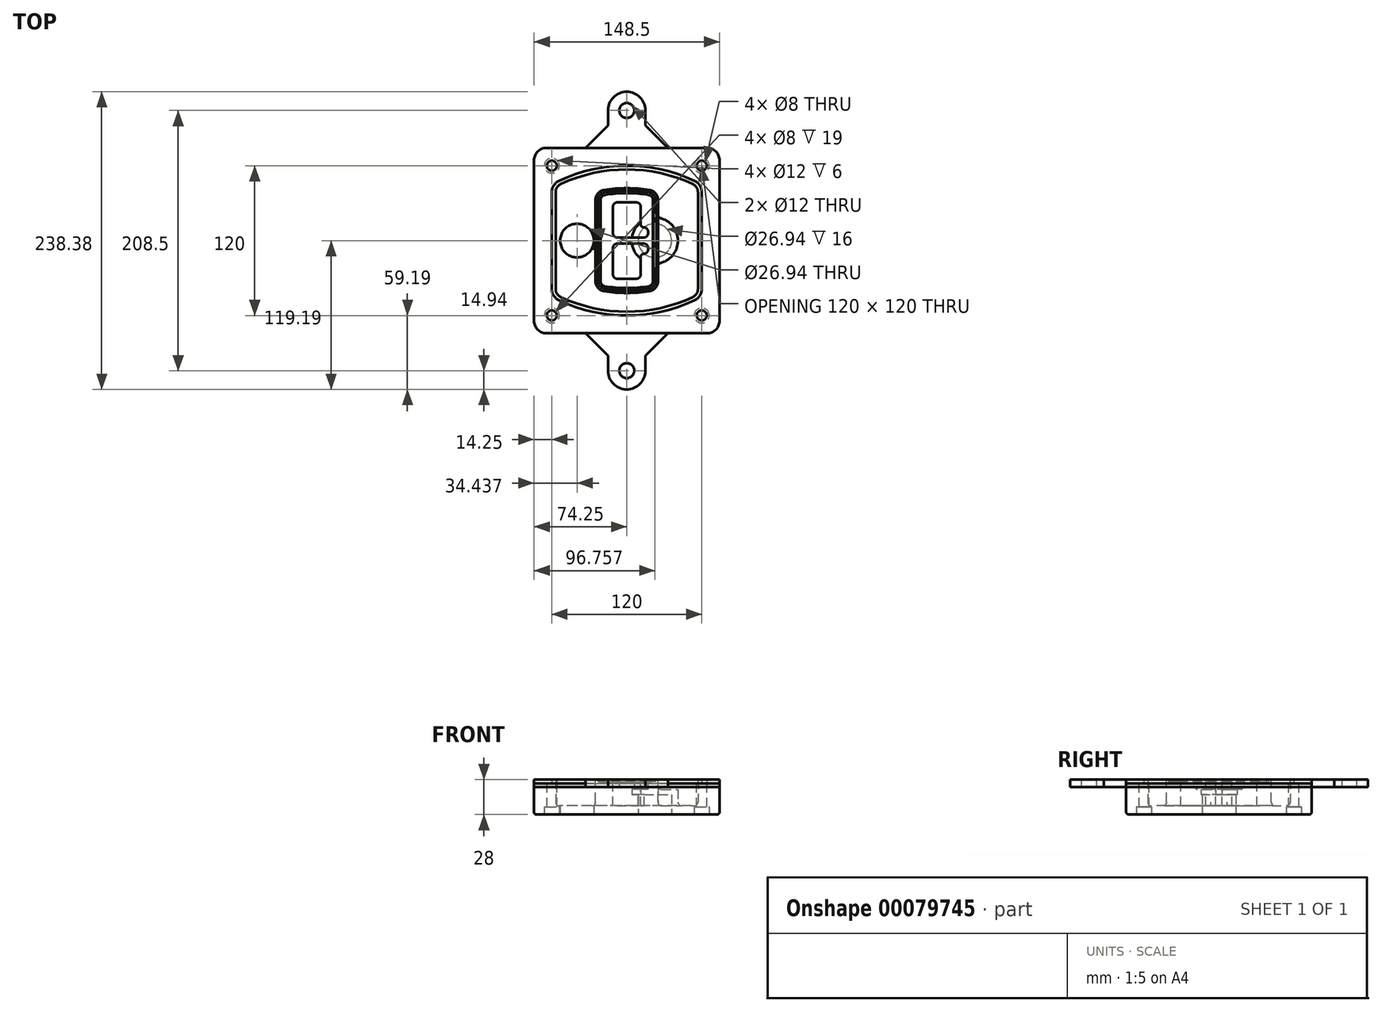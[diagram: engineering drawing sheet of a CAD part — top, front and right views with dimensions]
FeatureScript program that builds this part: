
annotation { "Feature Type Name" : "Feature", "Feature Type Description" : "" }
export const myFeature = defineFeature(function(context is Context, id is Id, definition is map)
    precondition{}
    {
        {
            var Q0;
            Q0=qCreatedBy(makeId("Top.planeOp"),FACE);
            var sketch = newSketch(context, id + "F0", { "sketchPlane" : qUnion([Q0])});
            skPoint(sketch, "E0.rect.middle", {"position": v(0, 0) * mm});
            skLineSegment(sketch, "E1.bottom", {"start": v(-64.25, -74.25) * mm, "end": v(64.25, -74.25) * mm});
            skLineSegment(sketch, "E1.top", {"start": v(-64.25, 74.25) * mm, "end": v(64.25, 74.25) * mm});
            skLineSegment(sketch, "E1.left", {"start": v(-74.25, -64.25) * mm, "end": v(-74.25, 64.25) * mm});
            skLineSegment(sketch, "E1.right", {"start": v(74.25, -64.25) * mm, "end": v(74.25, 64.25) * mm});
            skLineSegment(sketch, "E2", {"start": v(-74.25, 74.25) * mm, "end": v(74.25, -74.25) * mm, "construction": true});
            skLineSegment(sketch, "E3", {"start": v(74.25, 74.25) * mm, "end": v(-74.25, -74.25) * mm, "construction": true});
            skCircle(sketch, "E4", {"center": v(-60, 60) * mm, "radius": 4 * mm});
            skCircle(sketch, "E5", {"center": v(60, 60) * mm, "radius": 4 * mm});
            skCircle(sketch, "E6", {"center": v(60, -60) * mm, "radius": 4 * mm});
            skCircle(sketch, "E7", {"center": v(-60, -60) * mm, "radius": 4 * mm});
            skLineSegment(sketch, "E8", {"start": v(-60, 60) * mm, "end": v(60, 60) * mm, "construction": true});
            skLineSegment(sketch, "E9", {"start": v(60, 60) * mm, "end": v(60, -60) * mm, "construction": true});
            skLineSegment(sketch, "E10", {"start": v(60, -60) * mm, "end": v(-60, -60) * mm, "construction": true});
            skLineSegment(sketch, "E11", {"start": v(-60, -60) * mm, "end": v(-60, 60) * mm, "construction": true});
            skLineSegment(sketch, "E12", {"start": v(-60, 38.83) * mm, "end": v(-60, -38.83) * mm});
            skLineSegment(sketch, "E13", {"start": v(60, 38.83) * mm, "end": v(60, -38.83) * mm});
            skArc(sketch, "E14", {"start": v(54.26, 47.88) * mm, "mid": v(0, 60) * mm, "end": v(-54.26, 47.88) * mm});
            skArc(sketch, "E15", {"start": v(-54.26, -47.88) * mm, "mid": v(0, -60) * mm, "end": v(54.26, -47.88) * mm});
            skLineSegment(sketch, "E16", {"start": v(-60, 0) * mm, "end": v(60, 0) * mm, "construction": true});
            skPoint(sketch, "E17.visualSharp", {"position": v(-60, -45) * mm});
            skArc(sketch, "E17.filletArc", {"start": v(-60, -38.83) * mm, "mid": v(-58.44, -44.2) * mm, "end": v(-54.26, -47.88) * mm});
            skPoint(sketch, "E18.visualSharp", {"position": v(-60, 45) * mm});
            skArc(sketch, "E18.filletArc", {"start": v(-54.26, 47.88) * mm, "mid": v(-58.44, 44.2) * mm, "end": v(-60, 38.83) * mm});
            skPoint(sketch, "E19.visualSharp", {"position": v(60, 45) * mm});
            skArc(sketch, "E19.filletArc", {"start": v(60, 38.83) * mm, "mid": v(58.44, 44.2) * mm, "end": v(54.26, 47.88) * mm});
            skPoint(sketch, "E20.visualSharp", {"position": v(60, -45) * mm});
            skArc(sketch, "E20.filletArc", {"start": v(54.26, -47.88) * mm, "mid": v(58.44, -44.2) * mm, "end": v(60, -38.83) * mm});
            skPoint(sketch, "E21.visualSharp", {"position": v(-74.25, 74.25) * mm});
            skArc(sketch, "E21.filletArc", {"start": v(-64.25, 74.25) * mm, "mid": v(-71.32, 71.32) * mm, "end": v(-74.25, 64.25) * mm});
            skPoint(sketch, "E22.visualSharp", {"position": v(74.25, 74.25) * mm});
            skArc(sketch, "E22.filletArc", {"start": v(74.25, 64.25) * mm, "mid": v(71.32, 71.32) * mm, "end": v(64.25, 74.25) * mm});
            skPoint(sketch, "E23.visualSharp", {"position": v(74.25, -74.25) * mm});
            skArc(sketch, "E23.filletArc", {"start": v(64.25, -74.25) * mm, "mid": v(71.32, -71.32) * mm, "end": v(74.25, -64.25) * mm});
            skPoint(sketch, "E24.visualSharp", {"position": v(-74.25, -74.25) * mm});
            skArc(sketch, "E24.filletArc", {"start": v(-74.25, -64.25) * mm, "mid": v(-71.32, -71.32) * mm, "end": v(-64.25, -74.25) * mm});
            skArc(sketch, "E25.0", {"start": v(57, 38.83) * mm, "mid": v(55.9, 42.58) * mm, "end": v(52.98, 45.17) * mm});
            skLineSegment(sketch, "E25.1", {"start": v(57, 38.83) * mm, "end": v(57, -38.83) * mm});
            skArc(sketch, "E25.2", {"start": v(52.98, -45.17) * mm, "mid": v(55.9, -42.58) * mm, "end": v(57, -38.83) * mm});
            skArc(sketch, "E25.3", {"start": v(-52.98, -45.17) * mm, "mid": v(0, -57) * mm, "end": v(52.98, -45.17) * mm});
            skArc(sketch, "E25.4", {"start": v(-57, -38.83) * mm, "mid": v(-55.9, -42.58) * mm, "end": v(-52.98, -45.17) * mm});
            skArc(sketch, "E25.5", {"start": v(52.98, 45.17) * mm, "mid": v(0, 57) * mm, "end": v(-52.98, 45.17) * mm});
            skLineSegment(sketch, "E25.6", {"start": v(-57, 38.83) * mm, "end": v(-57, -38.83) * mm});
            skArc(sketch, "E25.7", {"start": v(-52.98, 45.17) * mm, "mid": v(-55.9, 42.58) * mm, "end": v(-57, 38.83) * mm});
            skArc(sketch, "E26.0", {"start": v(-55.96, 51.5) * mm, "mid": v(-61.82, 46.33) * mm, "end": v(-64, 38.83) * mm});
            skArc(sketch, "E26.1", {"start": v(55.96, 51.5) * mm, "mid": v(0, 64) * mm, "end": v(-55.96, 51.5) * mm});
            skArc(sketch, "E26.2", {"start": v(64, 38.83) * mm, "mid": v(61.82, 46.33) * mm, "end": v(55.96, 51.5) * mm});
            skLineSegment(sketch, "E26.3", {"start": v(64, 38.83) * mm, "end": v(64, -38.83) * mm});
            skArc(sketch, "E26.4", {"start": v(55.96, -51.5) * mm, "mid": v(61.82, -46.33) * mm, "end": v(64, -38.83) * mm});
            skLineSegment(sketch, "E26.5", {"start": v(-64, 38.83) * mm, "end": v(-64, -38.83) * mm});
            skArc(sketch, "E26.6", {"start": v(-55.96, -51.5) * mm, "mid": v(0, -64) * mm, "end": v(55.96, -51.5) * mm});
            skArc(sketch, "E26.7", {"start": v(-64, -38.83) * mm, "mid": v(-61.82, -46.33) * mm, "end": v(-55.96, -51.5) * mm});
            skSolve(sketch);
        }
        {
            var Q0;
            Q0=makeQuery(id+"F0.imprint","IMPRINT",FACE,{"disambiguationData":[TD([[makeQuery(id+"F0.imprint","IMPRINT",EDGE,{"derivedFrom":sQuery(id+"F0.wireOp",EDGE,"E1.bottom")}),1.0]])]});
            var Q1;
            Q1=makeQuery(id+"F0.imprint","IMPRINT",FACE,{"disambiguationData":[TD([[makeQuery(id+"F0.imprint","IMPRINT",EDGE,{"derivedFrom":sQuery(id+"F0.wireOp",EDGE,"E12")}),1.0]])]});
            var Q2;
            Q2=makeQuery(id+"F0.imprint","IMPRINT",FACE,{"disambiguationData":[TD([[makeQuery(id+"F0.imprint","IMPRINT",EDGE,{"derivedFrom":sQuery(id+"F0.wireOp",EDGE,"E25.0")}),1.0]])]});
            var Q3;
            Q3=makeQuery(id+"F0.imprint","IMPRINT",FACE,{"disambiguationData":[TD([[makeQuery(id+"F0.imprint","IMPRINT",EDGE,{"derivedFrom":sQuery(id+"F0.wireOp",EDGE,"E12")}),-1.0]])]});
            extrude(context, id + "F1", {"entities" : qUnion([Q0, Q1, Q2, Q3]), "oppositeDirection" : true, "depth" : 25 * mm});
        }
        {
            var Q0;
            Q0=makeQuery(id+"F0.imprint","IMPRINT",FACE,{"disambiguationData":[TD([[makeQuery(id+"F0.imprint","IMPRINT",EDGE,{"derivedFrom":sQuery(id+"F0.wireOp",EDGE,"E12")}),1.0]])]});
            extrude(context, id + "F2", {"entities" : qUnion([Q0]), "operationType" : NewBodyOperationType.ADD, "depth" : 3 * mm});
        }
        {
            var Q0;
            Q0=makeQuery(id+"F0.imprint","IMPRINT",FACE,{"disambiguationData":[TD([[makeQuery(id+"F0.imprint","IMPRINT",EDGE,{"derivedFrom":sQuery(id+"F0.wireOp",EDGE,"E25.0")}),1.0]])]});
            extrude(context, id + "F3", {"entities" : qUnion([Q0]), "operationType" : NewBodyOperationType.REMOVE, "oppositeDirection" : true, "depth" : 18 * mm});
        }
        {
            var Q0;
            Q0=makeQuery(id+"F2.opExtrude","CAP_FACE",FACE,{"disambiguationData":[OSD([sQuery(id+"F0.wireOp",EDGE,"E12"),sQuery(id+"F0.wireOp",EDGE,"E13"),sQuery(id+"F0.wireOp",EDGE,"E14"),sQuery(id+"F0.wireOp",EDGE,"E15"),sQuery(id+"F0.wireOp",EDGE,"E17.filletArc"),sQuery(id+"F0.wireOp",EDGE,"E18.filletArc"),sQuery(id+"F0.wireOp",EDGE,"E19.filletArc"),sQuery(id+"F0.wireOp",EDGE,"E20.filletArc"),sQuery(id+"F0.wireOp",EDGE,"E25.0"),sQuery(id+"F0.wireOp",EDGE,"E25.1"),sQuery(id+"F0.wireOp",EDGE,"E25.2"),sQuery(id+"F0.wireOp",EDGE,"E25.3"),sQuery(id+"F0.wireOp",EDGE,"E25.4"),sQuery(id+"F0.wireOp",EDGE,"E25.5"),sQuery(id+"F0.wireOp",EDGE,"E25.6"),sQuery(id+"F0.wireOp",EDGE,"E25.7")])],"isStart":false});
            var sketch = newSketch(context, id + "F4", { "sketchPlane" : qUnion([Q0])});
            skArc(sketch, "E27.0", {"start": v(-18.34, -40.45) * mm, "mid": v(0, -42) * mm, "end": v(18.34, -40.45) * mm});
            skArc(sketch, "E28.0", {"start": v(18.34, 40.45) * mm, "mid": v(0, 42) * mm, "end": v(-18.34, 40.45) * mm});
            skLineSegment(sketch, "E29", {"start": v(-25, 32.57) * mm, "end": v(-25, -32.57) * mm});
            skLineSegment(sketch, "E30", {"start": v(25, 32.57) * mm, "end": v(25, -32.57) * mm});
            skLineSegment(sketch, "E31", {"start": v(-25, 39.1) * mm, "end": v(25, 39.1) * mm, "construction": true});
            skLineSegment(sketch, "E32", {"start": v(-25, -39.1) * mm, "end": v(25, -39.1) * mm, "construction": true});
            skPoint(sketch, "E33.visualSharp", {"position": v(-25, 39.1) * mm});
            skArc(sketch, "E33.filletArc", {"start": v(-18.34, 40.45) * mm, "mid": v(-23.11, 37.73) * mm, "end": v(-25, 32.57) * mm});
            skPoint(sketch, "E34.visualSharp", {"position": v(25, 39.1) * mm});
            skArc(sketch, "E34.filletArc", {"start": v(25, 32.57) * mm, "mid": v(23.11, 37.73) * mm, "end": v(18.34, 40.45) * mm});
            skPoint(sketch, "E35.visualSharp", {"position": v(25, -39.1) * mm});
            skArc(sketch, "E35.filletArc", {"start": v(18.34, -40.45) * mm, "mid": v(23.11, -37.73) * mm, "end": v(25, -32.57) * mm});
            skPoint(sketch, "E36.visualSharp", {"position": v(-25, -39.1) * mm});
            skArc(sketch, "E36.filletArc", {"start": v(-25, -32.57) * mm, "mid": v(-23.11, -37.73) * mm, "end": v(-18.34, -40.45) * mm});
            skArc(sketch, "E37.0", {"start": v(52.98, 45.17) * mm, "mid": v(0, 57) * mm, "end": v(-52.98, 45.17) * mm});
            skArc(sketch, "E37.1", {"start": v(-52.98, 45.17) * mm, "mid": v(-55.9, 42.58) * mm, "end": v(-57, 38.83) * mm});
            skLineSegment(sketch, "E37.2", {"start": v(-57, 38.83) * mm, "end": v(-57, -38.83) * mm});
            skArc(sketch, "E37.3", {"start": v(-57, -38.83) * mm, "mid": v(-55.9, -42.58) * mm, "end": v(-52.98, -45.17) * mm});
            skArc(sketch, "E37.4", {"start": v(-52.98, -45.17) * mm, "mid": v(0, -57) * mm, "end": v(52.98, -45.17) * mm});
            skArc(sketch, "E37.5", {"start": v(52.98, -45.17) * mm, "mid": v(55.9, -42.58) * mm, "end": v(57, -38.83) * mm});
            skLineSegment(sketch, "E37.6", {"start": v(57, 38.83) * mm, "end": v(57, -38.83) * mm});
            skArc(sketch, "E37.7", {"start": v(57, 38.83) * mm, "mid": v(55.9, 42.58) * mm, "end": v(52.98, 45.17) * mm});
            skLineSegment(sketch, "E38.0", {"start": v(23, 32.57) * mm, "end": v(23, -32.57) * mm});
            skArc(sketch, "E38.1", {"start": v(18, -38.48) * mm, "mid": v(21.58, -36.44) * mm, "end": v(23, -32.57) * mm});
            skArc(sketch, "E38.2", {"start": v(-18, -38.48) * mm, "mid": v(0, -40) * mm, "end": v(18, -38.48) * mm});
            skArc(sketch, "E38.3", {"start": v(-23, -32.57) * mm, "mid": v(-21.58, -36.44) * mm, "end": v(-18, -38.48) * mm});
            skLineSegment(sketch, "E38.4", {"start": v(-23, 32.57) * mm, "end": v(-23, -32.57) * mm});
            skArc(sketch, "E38.5", {"start": v(23, 32.57) * mm, "mid": v(21.58, 36.44) * mm, "end": v(18, 38.48) * mm});
            skArc(sketch, "E38.6", {"start": v(-18, 38.48) * mm, "mid": v(-21.58, 36.44) * mm, "end": v(-23, 32.57) * mm});
            skArc(sketch, "E38.7", {"start": v(18, 38.48) * mm, "mid": v(0, 40) * mm, "end": v(-18, 38.48) * mm});
            skArc(sketch, "E39.0", {"start": v(21, 32.57) * mm, "mid": v(20.06, 35.15) * mm, "end": v(17.67, 36.5) * mm});
            skLineSegment(sketch, "E39.1", {"start": v(21, 32.57) * mm, "end": v(21, -32.57) * mm});
            skArc(sketch, "E39.2", {"start": v(17.67, -36.5) * mm, "mid": v(20.06, -35.15) * mm, "end": v(21, -32.57) * mm});
            skArc(sketch, "E39.3", {"start": v(-17.67, -36.5) * mm, "mid": v(0, -38) * mm, "end": v(17.67, -36.5) * mm});
            skArc(sketch, "E39.4", {"start": v(-21, -32.57) * mm, "mid": v(-20.06, -35.15) * mm, "end": v(-17.67, -36.5) * mm});
            skArc(sketch, "E39.5", {"start": v(17.67, 36.5) * mm, "mid": v(0, 38) * mm, "end": v(-17.67, 36.5) * mm});
            skLineSegment(sketch, "E39.6", {"start": v(-21, 32.57) * mm, "end": v(-21, -32.57) * mm});
            skArc(sketch, "E39.7", {"start": v(-17.67, 36.5) * mm, "mid": v(-20.06, 35.15) * mm, "end": v(-21, 32.57) * mm});
            skLineSegment(sketch, "E40", {"start": v(-25, 0) * mm, "end": v(25, 0) * mm, "construction": true});
            skLineSegment(sketch, "E41", {"start": v(-11, 5.5) * mm, "end": v(-11, 27.5) * mm});
            skLineSegment(sketch, "E42", {"start": v(-8, 30.5) * mm, "end": v(8, 30.5) * mm});
            skLineSegment(sketch, "E43", {"start": v(11, 27.5) * mm, "end": v(11, 13.5) * mm});
            skLineSegment(sketch, "E44", {"start": v(14, 10.5) * mm, "end": v(14, 10.5) * mm});
            skLineSegment(sketch, "E45", {"start": v(17, 7.5) * mm, "end": v(17, 5.5) * mm});
            skLineSegment(sketch, "E46", {"start": v(14, 2.5) * mm, "end": v(-8, 2.5) * mm});
            skPoint(sketch, "E47.visualSharp", {"position": v(-11, 30.5) * mm});
            skArc(sketch, "E47.filletArc", {"start": v(-8, 30.5) * mm, "mid": v(-10.12, 29.62) * mm, "end": v(-11, 27.5) * mm});
            skPoint(sketch, "E48.visualSharp", {"position": v(11, 30.5) * mm});
            skArc(sketch, "E48.filletArc", {"start": v(11, 27.5) * mm, "mid": v(10.12, 29.62) * mm, "end": v(8, 30.5) * mm});
            skPoint(sketch, "E49.visualSharp", {"position": v(11, 10.5) * mm});
            skArc(sketch, "E49.filletArc", {"start": v(11, 13.5) * mm, "mid": v(11.88, 11.38) * mm, "end": v(14, 10.5) * mm});
            skPoint(sketch, "E50.visualSharp", {"position": v(17, 10.5) * mm});
            skArc(sketch, "E50.filletArc", {"start": v(17, 7.5) * mm, "mid": v(16.12, 9.62) * mm, "end": v(14, 10.5) * mm});
            skPoint(sketch, "E51.visualSharp", {"position": v(17, 2.5) * mm});
            skArc(sketch, "E51.filletArc", {"start": v(14, 2.5) * mm, "mid": v(16.12, 3.38) * mm, "end": v(17, 5.5) * mm});
            skPoint(sketch, "E52.visualSharp", {"position": v(-11, 2.5) * mm});
            skArc(sketch, "E52.filletArc", {"start": v(-11, 5.5) * mm, "mid": v(-10.12, 3.38) * mm, "end": v(-8, 2.5) * mm});
            skLineSegment(sketch, "E53.0.MirrorCS", {"start": v(14, -2.5) * mm, "end": v(-8, -2.5) * mm});
            skArc(sketch, "E54.0.MirrorCS", {"start": v(-11, -5.5) * mm, "mid": v(-10.12, -3.38) * mm, "end": v(-8, -2.5) * mm});
            skLineSegment(sketch, "E55.0.MirrorCS", {"start": v(-11, -5.5) * mm, "end": v(-11, -27.5) * mm});
            skArc(sketch, "E56.0.MirrorCS", {"start": v(-8, -30.5) * mm, "mid": v(-10.12, -29.62) * mm, "end": v(-11, -27.5) * mm});
            skLineSegment(sketch, "E57.0.MirrorCS", {"start": v(-8, -30.5) * mm, "end": v(8, -30.5) * mm});
            skArc(sketch, "E58.0.MirrorCS", {"start": v(11, -27.5) * mm, "mid": v(10.12, -29.62) * mm, "end": v(8, -30.5) * mm});
            skLineSegment(sketch, "E59.0.MirrorCS", {"start": v(11, -27.5) * mm, "end": v(11, -13.5) * mm});
            skArc(sketch, "E60.0.MirrorCS", {"start": v(11, -13.5) * mm, "mid": v(11.88, -11.38) * mm, "end": v(14, -10.5) * mm});
            skArc(sketch, "E61.0.MirrorCS", {"start": v(17, -7.5) * mm, "mid": v(16.12, -9.62) * mm, "end": v(14, -10.5) * mm});
            skLineSegment(sketch, "E62.0.MirrorCS", {"start": v(17, -7.5) * mm, "end": v(17, -5.5) * mm});
            skArc(sketch, "E63.0.MirrorCS", {"start": v(14, -2.5) * mm, "mid": v(16.12, -3.38) * mm, "end": v(17, -5.5) * mm});
            skSolve(sketch);
        }
        {
            var Q0;
            Q0=makeQuery(id+"F4.imprint","IMPRINT",FACE,{"disambiguationData":[TD([[makeQuery(id+"F4.imprint","IMPRINT",EDGE,{"derivedFrom":sQuery(id+"F4.wireOp",EDGE,"E27.0")}),1.0]])]});
            var Q1;
            Q1=makeQuery(id+"F4.imprint","IMPRINT",FACE,{"disambiguationData":[TD([[makeQuery(id+"F4.imprint","IMPRINT",EDGE,{"derivedFrom":sQuery(id+"F4.wireOp",EDGE,"E38.0")}),-1.0]])]});
            var Q2;
            Q2=makeQuery(id+"F4.imprint","IMPRINT",FACE,{"disambiguationData":[TD([[makeQuery(id+"F4.imprint","IMPRINT",EDGE,{"derivedFrom":sQuery(id+"F4.wireOp",EDGE,"E39.0")}),1.0]])]});
            extrude(context, id + "F5", {"entities" : qUnion([Q0, Q1, Q2]), "operationType" : NewBodyOperationType.ADD, "endBound" : BoundingType.UP_TO_NEXT, "oppositeDirection" : true, "depth" : 25 * mm});
        }
        {
            var Q0;
            Q0=makeQuery(id+"F4.imprint","IMPRINT",FACE,{"disambiguationData":[TD([[makeQuery(id+"F4.imprint","IMPRINT",EDGE,{"derivedFrom":sQuery(id+"F4.wireOp",EDGE,"E38.0")}),-1.0]])]});
            extrude(context, id + "F6", {"entities" : qUnion([Q0]), "operationType" : NewBodyOperationType.REMOVE, "oppositeDirection" : true, "depth" : 2 * mm});
        }
        {
            var Q0;
            Q0=makeQuery(id+"F1.opExtrude","CAP_FACE",FACE,{"disambiguationData":[OSD([sQuery(id+"F0.wireOp",EDGE,"E1.bottom"),sQuery(id+"F0.wireOp",EDGE,"E1.top"),sQuery(id+"F0.wireOp",EDGE,"E1.left"),sQuery(id+"F0.wireOp",EDGE,"E1.right"),sQuery(id+"F0.wireOp",EDGE,"E4"),sQuery(id+"F0.wireOp",EDGE,"E5"),sQuery(id+"F0.wireOp",EDGE,"E6"),sQuery(id+"F0.wireOp",EDGE,"E7"),sQuery(id+"F0.wireOp",EDGE,"E21.filletArc"),sQuery(id+"F0.wireOp",EDGE,"E22.filletArc"),sQuery(id+"F0.wireOp",EDGE,"E23.filletArc"),sQuery(id+"F0.wireOp",EDGE,"E24.filletArc")])],"isStart":false});
            var sketch = newSketch(context, id + "F7", { "sketchPlane" : qUnion([Q0])});
            skCircle(sketch, "E64", {"center": v(22.5, 0) * mm, "radius": 13.47 * mm});
            skCircle(sketch, "E65", {"center": v(-39.81, 0) * mm, "radius": 13.47 * mm});
            skLineSegment(sketch, "E66", {"start": v(74.25, 0) * mm, "end": v(-74.25, 0) * mm});
            skCircle(sketch, "E67", {"center": v(22.5, 0) * mm, "radius": 18.47 * mm});
            skCircle(sketch, "E68", {"center": v(60, -60) * mm, "radius": 6 * mm});
            skCircle(sketch, "E69", {"center": v(-60, -60) * mm, "radius": 6 * mm});
            skCircle(sketch, "E70", {"center": v(-60, 60) * mm, "radius": 6 * mm});
            skCircle(sketch, "E71", {"center": v(60, 60) * mm, "radius": 6 * mm});
            skSolve(sketch);
        }
        {
            var Q0;
            {var subQ1=sQuery(id+"F7.wireOp",EDGE,"E66");var subQ4=sQuery(id+"F7.wireOp",EDGE,"E64");var subQ6=makeQuery(id+"F7.imprint","INTERSECT",VERTEX,{"disambiguationData":[OD(0.0)],"derivedFrom":[subQ4,subQ1]});Q0=makeQuery(id+"F7.imprint","IMPRINT",FACE,{"disambiguationData":[TD([[makeQuery(id+"F7.imprint","IMPRINT",EDGE,{"disambiguationData":[TD([[subQ6,-1.0]])],"derivedFrom":subQ4}),-1.0]])]});}
            var Q1;
            {var subQ0=sQuery(id+"F7.wireOp",EDGE,"E66");var subQ1=sQuery(id+"F7.wireOp",EDGE,"E64");var subQ3=makeQuery(id+"F7.imprint","INTERSECT",VERTEX,{"disambiguationData":[OD(0.0)],"derivedFrom":[subQ1,subQ0]});Q1=makeQuery(id+"F7.imprint","IMPRINT",FACE,{"disambiguationData":[TD([[makeQuery(id+"F7.imprint","IMPRINT",EDGE,{"disambiguationData":[TD([[subQ3,-1.0]])],"derivedFrom":subQ1}),1.0]])]});}
            var Q2;
            {var subQ0=sQuery(id+"F7.wireOp",EDGE,"E66");var subQ1=sQuery(id+"F7.wireOp",EDGE,"E64");var subQ3=makeQuery(id+"F7.imprint","INTERSECT",VERTEX,{"disambiguationData":[OD(0.0)],"derivedFrom":[subQ1,subQ0]});Q2=makeQuery(id+"F7.imprint","IMPRINT",FACE,{"disambiguationData":[TD([[makeQuery(id+"F7.imprint","IMPRINT",EDGE,{"disambiguationData":[TD([[subQ3,1.0]])],"derivedFrom":subQ1}),1.0]])]});}
            var Q3;
            {var subQ1=sQuery(id+"F7.wireOp",EDGE,"E66");var subQ4=sQuery(id+"F7.wireOp",EDGE,"E64");var subQ6=makeQuery(id+"F7.imprint","INTERSECT",VERTEX,{"disambiguationData":[OD(0.0)],"derivedFrom":[subQ4,subQ1]});Q3=makeQuery(id+"F7.imprint","IMPRINT",FACE,{"disambiguationData":[TD([[makeQuery(id+"F7.imprint","IMPRINT",EDGE,{"disambiguationData":[TD([[subQ6,1.0]])],"derivedFrom":subQ4}),-1.0]])]});}
            extrude(context, id + "F8", {"entities" : qUnion([Q0, Q1, Q2, Q3]), "operationType" : NewBodyOperationType.ADD, "oppositeDirection" : true, "depth" : 20 * mm});
        }
        {
            var Q0;
            {var subQ0=sQuery(id+"F7.wireOp",EDGE,"E66");var subQ1=sQuery(id+"F7.wireOp",EDGE,"E64");var subQ3=makeQuery(id+"F7.imprint","INTERSECT",VERTEX,{"disambiguationData":[OD(0.0)],"derivedFrom":[subQ1,subQ0]});Q0=makeQuery(id+"F7.imprint","IMPRINT",FACE,{"disambiguationData":[TD([[makeQuery(id+"F7.imprint","IMPRINT",EDGE,{"disambiguationData":[TD([[subQ3,-1.0]])],"derivedFrom":subQ1}),1.0]])]});}
            var Q1;
            {var subQ0=sQuery(id+"F7.wireOp",EDGE,"E66");var subQ1=sQuery(id+"F7.wireOp",EDGE,"E64");var subQ3=makeQuery(id+"F7.imprint","INTERSECT",VERTEX,{"disambiguationData":[OD(0.0)],"derivedFrom":[subQ1,subQ0]});Q1=makeQuery(id+"F7.imprint","IMPRINT",FACE,{"disambiguationData":[TD([[makeQuery(id+"F7.imprint","IMPRINT",EDGE,{"disambiguationData":[TD([[subQ3,1.0]])],"derivedFrom":subQ1}),1.0]])]});}
            extrude(context, id + "F9", {"entities" : qUnion([Q0, Q1]), "operationType" : NewBodyOperationType.REMOVE, "oppositeDirection" : true, "depth" : 16 * mm});
        }
        {
            var Q0;
            {var subQ0=sQuery(id+"F7.wireOp",EDGE,"E66");var subQ1=sQuery(id+"F7.wireOp",EDGE,"E65");var subQ3=makeQuery(id+"F7.imprint","INTERSECT",VERTEX,{"disambiguationData":[OD(0.0)],"derivedFrom":[subQ1,subQ0]});Q0=makeQuery(id+"F7.imprint","IMPRINT",FACE,{"disambiguationData":[TD([[makeQuery(id+"F7.imprint","IMPRINT",EDGE,{"disambiguationData":[TD([[subQ3,-1.0]])],"derivedFrom":subQ1}),1.0]])]});}
            var Q1;
            {var subQ0=sQuery(id+"F7.wireOp",EDGE,"E66");var subQ1=sQuery(id+"F7.wireOp",EDGE,"E65");var subQ3=makeQuery(id+"F7.imprint","INTERSECT",VERTEX,{"disambiguationData":[OD(0.0)],"derivedFrom":[subQ1,subQ0]});Q1=makeQuery(id+"F7.imprint","IMPRINT",FACE,{"disambiguationData":[TD([[makeQuery(id+"F7.imprint","IMPRINT",EDGE,{"disambiguationData":[TD([[subQ3,1.0]])],"derivedFrom":subQ1}),1.0]])]});}
            extrude(context, id + "F10", {"entities" : qUnion([Q0, Q1]), "operationType" : NewBodyOperationType.REMOVE, "oppositeDirection" : true, "depth" : 25 * mm});
        }
        {
            var Q0;
            Q0=makeQuery(id+"F7.imprint","IMPRINT",FACE,{"disambiguationData":[TD([[makeQuery(id+"F7.imprint","IMPRINT",EDGE,{"derivedFrom":sQuery(id+"F7.wireOp",EDGE,"E68")}),1.0]])]});
            var Q1;
            Q1=makeQuery(id+"F7.imprint","IMPRINT",FACE,{"disambiguationData":[TD([[makeQuery(id+"F7.imprint","IMPRINT",EDGE,{"derivedFrom":makeQuery(id+"F1.opExtrude","CAP_EDGE",EDGE,{"disambiguationData":[OSD([sQuery(id+"F0.wireOp",EDGE,"E5")])],"isStart":false})}),-1.0]])]});
            var Q2;
            Q2=makeQuery(id+"F7.imprint","IMPRINT",FACE,{"disambiguationData":[TD([[makeQuery(id+"F7.imprint","IMPRINT",EDGE,{"derivedFrom":sQuery(id+"F7.wireOp",EDGE,"E69")}),1.0]])]});
            var Q3;
            Q3=makeQuery(id+"F7.imprint","IMPRINT",FACE,{"disambiguationData":[TD([[makeQuery(id+"F7.imprint","IMPRINT",EDGE,{"derivedFrom":makeQuery(id+"F1.opExtrude","CAP_EDGE",EDGE,{"disambiguationData":[OSD([sQuery(id+"F0.wireOp",EDGE,"E4")])],"isStart":false})}),-1.0]])]});
            var Q4;
            Q4=makeQuery(id+"F7.imprint","IMPRINT",FACE,{"disambiguationData":[TD([[makeQuery(id+"F7.imprint","IMPRINT",EDGE,{"derivedFrom":sQuery(id+"F7.wireOp",EDGE,"E70")}),1.0]])]});
            var Q5;
            Q5=makeQuery(id+"F7.imprint","IMPRINT",FACE,{"disambiguationData":[TD([[makeQuery(id+"F7.imprint","IMPRINT",EDGE,{"derivedFrom":makeQuery(id+"F1.opExtrude","CAP_EDGE",EDGE,{"disambiguationData":[OSD([sQuery(id+"F0.wireOp",EDGE,"E7")])],"isStart":false})}),-1.0]])]});
            var Q6;
            Q6=makeQuery(id+"F7.imprint","IMPRINT",FACE,{"disambiguationData":[TD([[makeQuery(id+"F7.imprint","IMPRINT",EDGE,{"derivedFrom":sQuery(id+"F7.wireOp",EDGE,"E71")}),1.0]])]});
            var Q7;
            Q7=makeQuery(id+"F7.imprint","IMPRINT",FACE,{"disambiguationData":[TD([[makeQuery(id+"F7.imprint","IMPRINT",EDGE,{"derivedFrom":makeQuery(id+"F1.opExtrude","CAP_EDGE",EDGE,{"disambiguationData":[OSD([sQuery(id+"F0.wireOp",EDGE,"E6")])],"isStart":false})}),-1.0]])]});
            extrude(context, id + "F11", {"entities" : qUnion([Q0, Q1, Q2, Q3, Q4, Q5, Q6, Q7]), "operationType" : NewBodyOperationType.REMOVE, "oppositeDirection" : true, "depth" : 6 * mm});
        }
        {
            var Q0;
            Q0=makeQuery(id+"F9.boolean.opBoolean","COPY",FACE,{"derivedFrom":makeQuery(id+"F9.opExtrude","CAP_FACE",FACE,{"disambiguationData":[OSD([sQuery(id+"F7.wireOp",EDGE,"E64")])],"isStart":false})});
            var sketch = newSketch(context, id + "F12", { "sketchPlane" : qUnion([Q0])});
            skArc(sketch, "E72.0", {"start": v(11, 14.45) * mm, "mid": v(6.45, 9.13) * mm, "end": v(4.2, 2.5) * mm});
            skArc(sketch, "E72.1", {"start": v(4.2, -2.5) * mm, "mid": v(6.45, -9.13) * mm, "end": v(11, -14.45) * mm});
            skLineSegment(sketch, "E73", {"start": v(4.2, -2.5) * mm, "end": v(14, -2.5) * mm});
            skLineSegment(sketch, "E74.0", {"start": v(14, 2.5) * mm, "end": v(4.2, 2.5) * mm});
            skArc(sketch, "E74.1", {"start": v(14, 2.5) * mm, "mid": v(16.12, 3.38) * mm, "end": v(17, 5.5) * mm});
            skLineSegment(sketch, "E74.2", {"start": v(17, 7.5) * mm, "end": v(17, 5.5) * mm});
            skArc(sketch, "E74.3", {"start": v(17, 7.5) * mm, "mid": v(16.12, 9.62) * mm, "end": v(14, 10.5) * mm});
            skArc(sketch, "E74.4", {"start": v(11, 13.5) * mm, "mid": v(11.88, 11.38) * mm, "end": v(14, 10.5) * mm});
            skLineSegment(sketch, "E74.5", {"start": v(11, 14.45) * mm, "end": v(11, 13.5) * mm});
            skLineSegment(sketch, "E74.7", {"start": v(14, -2.5) * mm, "end": v(4.2, -2.5) * mm});
            skArc(sketch, "E74.8", {"start": v(14, -2.5) * mm, "mid": v(16.12, -3.38) * mm, "end": v(17, -5.5) * mm});
            skLineSegment(sketch, "E74.9", {"start": v(17, -7.5) * mm, "end": v(17, -5.5) * mm});
            skArc(sketch, "E74.10", {"start": v(17, -7.5) * mm, "mid": v(16.12, -9.62) * mm, "end": v(14, -10.5) * mm});
            skArc(sketch, "E74.11", {"start": v(11, -13.5) * mm, "mid": v(11.88, -11.38) * mm, "end": v(14, -10.5) * mm});
            skLineSegment(sketch, "E74.12", {"start": v(11, -14.45) * mm, "end": v(11, -13.5) * mm});
            skPoint(sketch, "E75.orphan", {"position": v(11, -27.5) * mm});
            skPoint(sketch, "E76.orphan", {"position": v(-8, -2.5) * mm});
            skPoint(sketch, "E77.orphan", {"position": v(-8, 2.5) * mm});
            skPoint(sketch, "E78.orphan", {"position": v(11, 27.5) * mm});
            skSolve(sketch);
        }
        {
            var Q0;
            {var subQ7=sQuery(id+"F12.wireOp",EDGE,"E72.0");var subQ14=sQuery(id+"F12.wireOp",EDGE,"E72.1");var subQ16=sQuery(id+"F12.wireOp",EDGE,"E74.1");var subQ18=sQuery(id+"F12.wireOp",EDGE,"E74.8");Q0=qUnion([makeQuery(id+"F12.imprint","IMPRINT",FACE,{"disambiguationData":[TD([[makeQuery(id+"F12.imprint","IMPRINT",EDGE,{"derivedFrom":subQ7}),1.0]])]}),makeQuery(id+"F12.imprint","IMPRINT",FACE,{"disambiguationData":[TD([[makeQuery(id+"F12.imprint","IMPRINT",EDGE,{"derivedFrom":subQ14}),1.0]])]}),makeQuery(id+"F12.imprint","IMPRINT",FACE,{"disambiguationData":[TD([[makeQuery(id+"F12.imprint","IMPRINT",EDGE,{"derivedFrom":subQ16}),1.0]])]}),makeQuery(id+"F12.imprint","IMPRINT",FACE,{"disambiguationData":[TD([[makeQuery(id+"F12.imprint","IMPRINT",EDGE,{"derivedFrom":subQ18}),-1.0]])]})]);}
            var Q1;
            Q1=makeQuery(id+"F5.boolean.opBoolean","SPLIT",FACE,{"disambiguationData":[TD([makeQuery(id+"F5.opExtrude","SWEPT_FACE",FACE,{"disambiguationData":[OSD([sQuery(id+"F4.wireOp",EDGE,"E41")])]})])],"derivedFrom":makeQuery(id+"F3.boolean.opBoolean","COPY",FACE,{"derivedFrom":makeQuery(id+"F3.opExtrude","CAP_FACE",FACE,{"disambiguationData":[OSD([sQuery(id+"F0.wireOp",EDGE,"E25.0"),sQuery(id+"F0.wireOp",EDGE,"E25.1"),sQuery(id+"F0.wireOp",EDGE,"E25.2"),sQuery(id+"F0.wireOp",EDGE,"E25.3"),sQuery(id+"F0.wireOp",EDGE,"E25.4"),sQuery(id+"F0.wireOp",EDGE,"E25.5"),sQuery(id+"F0.wireOp",EDGE,"E25.6"),sQuery(id+"F0.wireOp",EDGE,"E25.7")])],"isStart":false})})});
            extrude(context, id + "F13", {"entities" : qUnion([Q0]), "operationType" : NewBodyOperationType.REMOVE, "endBound" : BoundingType.UP_TO_SURFACE, "endBoundEntityFace" : qUnion([Q1]), "depth" : 25 * mm});
        }
        {
            var Q0;
            Q0=makeQuery(id+"F3.boolean.opBoolean","COPY",EDGE,{"derivedFrom":makeQuery(id+"F3.opExtrude","CAP_EDGE",EDGE,{"disambiguationData":[OSD([sQuery(id+"F0.wireOp",EDGE,"E25.6")])],"isStart":false})});
            var Q1;
            Q1=makeQuery(id+"F8.boolean.opBoolean","INTERSECT",EDGE,{"derivedFrom":[makeQuery(id+"F5.opExtrude","SWEPT_FACE",FACE,{"disambiguationData":[OSD([sQuery(id+"F4.wireOp",EDGE,"E30")])]}),makeQuery(id+"F8.opExtrude","CAP_FACE",FACE,{"disambiguationData":[OSD([sQuery(id+"F7.wireOp",EDGE,"E67")])],"isStart":false})]});
            var Q2;
            Q2=makeQuery(id+"F8.boolean.opBoolean","INTERSECT",EDGE,{"disambiguationData":[OD(1.0)],"derivedFrom":[makeQuery(id+"F5.opExtrude","SWEPT_FACE",FACE,{"disambiguationData":[OSD([sQuery(id+"F4.wireOp",EDGE,"E30")])]}),makeQuery(id+"F8.opExtrude","SWEPT_FACE",FACE,{"disambiguationData":[OSD([sQuery(id+"F7.wireOp",EDGE,"E67")])]})]});
            var Q3;
            {var subQ0=sQuery(id+"F4.wireOp",EDGE,"E30");Q3=makeQuery(id+"F8.boolean.opBoolean","SPLIT",EDGE,{"disambiguationData":[TD([makeQuery(id+"F5.opExtrude","SWEPT_FACE",FACE,{"disambiguationData":[OSD([sQuery(id+"F4.wireOp",EDGE,"E35.filletArc")])]})])],"derivedFrom":makeQuery(id+"F5.opExtrude","CAP_EDGE",EDGE,{"disambiguationData":[OSD([subQ0])],"isStart":false})});}
            var Q4;
            {var subQ0=sQuery(id+"F0.wireOp",EDGE,"E25.7");var subQ1=sQuery(id+"F0.wireOp",EDGE,"E25.1");var subQ2=sQuery(id+"F0.wireOp",EDGE,"E25.6");var subQ3=sQuery(id+"F0.wireOp",EDGE,"E25.5");var subQ4=sQuery(id+"F0.wireOp",EDGE,"E25.4");var subQ5=sQuery(id+"F0.wireOp",EDGE,"E25.0");var subQ6=sQuery(id+"F0.wireOp",EDGE,"E25.2");var subQ7=sQuery(id+"F0.wireOp",EDGE,"E25.3");Q4=makeQuery(id+"F8.boolean.opBoolean","INTERSECT",EDGE,{"derivedFrom":[makeQuery(id+"F5.boolean.opBoolean","SPLIT",FACE,{"disambiguationData":[TD([makeQuery(id+"F2.opExtrude","SWEPT_FACE",FACE,{"disambiguationData":[OSD([subQ5])]})])],"derivedFrom":makeQuery(id+"F3.boolean.opBoolean","COPY",FACE,{"derivedFrom":makeQuery(id+"F3.opExtrude","CAP_FACE",FACE,{"disambiguationData":[OSD([subQ5,subQ1,subQ6,subQ7,subQ4,subQ3,subQ2,subQ0])],"isStart":false})})}),makeQuery(id+"F8.opExtrude","SWEPT_FACE",FACE,{"disambiguationData":[OSD([sQuery(id+"F7.wireOp",EDGE,"E67")])]})]});}
            var Q5;
            Q5=makeQuery(id+"F8.boolean.opBoolean","INTERSECT",EDGE,{"disambiguationData":[OD(0.0)],"derivedFrom":[makeQuery(id+"F5.opExtrude","SWEPT_FACE",FACE,{"disambiguationData":[OSD([sQuery(id+"F4.wireOp",EDGE,"E30")])]}),makeQuery(id+"F8.opExtrude","SWEPT_FACE",FACE,{"disambiguationData":[OSD([sQuery(id+"F7.wireOp",EDGE,"E67")])]})]});
            fillet(context, id + "F14", {"entities" : qUnion([Q0, Q1, Q2, Q3, Q4, Q5]), "radius" : 3 * mm, "tangentPropagation" : true, "allowEdgeOverflow" : false});
        }
        {
            var Q0;
            Q0=makeQuery(id+"F1.opExtrude","CAP_EDGE",EDGE,{"disambiguationData":[OSD([sQuery(id+"F0.wireOp",EDGE,"E1.bottom")])],"isStart":false});
            fillet(context, id + "F15", {"entities" : qUnion([Q0]), "radius" : 2 * mm, "tangentPropagation" : true, "allowEdgeOverflow" : false});
        }
        {
            var Q0;
            {var subQ0=sQuery(id+"F0.wireOp",EDGE,"E22.filletArc");var subQ1=sQuery(id+"F0.wireOp",EDGE,"E7");var subQ2=sQuery(id+"F0.wireOp",EDGE,"E6");var subQ3=sQuery(id+"F0.wireOp",EDGE,"E5");var subQ4=sQuery(id+"F0.wireOp",EDGE,"E4");var subQ5=sQuery(id+"F0.wireOp",EDGE,"E1.bottom");var subQ6=sQuery(id+"F0.wireOp",EDGE,"E21.filletArc");var subQ7=sQuery(id+"F0.wireOp",EDGE,"E1.top");var subQ8=sQuery(id+"F0.wireOp",EDGE,"E1.left");var subQ9=sQuery(id+"F0.wireOp",EDGE,"E1.right");var subQ10=sQuery(id+"F0.wireOp",EDGE,"E23.filletArc");var subQ11=sQuery(id+"F0.wireOp",EDGE,"E24.filletArc");Q0=makeQuery(id+"F2.boolean.opBoolean","SPLIT",FACE,{"disambiguationData":[TD([makeQuery(id+"F1.opExtrude","SWEPT_FACE",FACE,{"disambiguationData":[OSD([subQ5])]})])],"derivedFrom":makeQuery(id+"F1.opExtrude","CAP_FACE",FACE,{"disambiguationData":[OSD([subQ5,subQ7,subQ8,subQ9,subQ4,subQ3,subQ2,subQ1,subQ6,subQ0,subQ10,subQ11])],"isStart":true})});}
            var sketch = newSketch(context, id + "F16", { "sketchPlane" : qUnion([Q0])});
            skSolve(sketch);
        }
        {
            var Q0;
            Q0=makeQuery(id+"F16.imprint","IMPRINT",FACE,{"disambiguationData":[TD([[makeQuery(id+"F16.imprint","IMPRINT",EDGE,{"derivedFrom":makeQuery(id+"F1.opExtrude","CAP_EDGE",EDGE,{"disambiguationData":[OSD([sQuery(id+"F0.wireOp",EDGE,"E1.bottom")])],"isStart":true})}),1.0]])]});
            var sketch = newSketch(context, id + "F17", { "sketchPlane" : qUnion([Q0])});
            skLineSegment(sketch, "E79", {"start": v(0, 0) * mm, "end": v(0, 104.25) * mm, "construction": true});
            skCircle(sketch, "E80", {"center": v(0, 104.25) * mm, "radius": 6 * mm});
            skArc(sketch, "E81", {"start": v(14.96, 104.25) * mm, "mid": v(-0.04, 119.2) * mm, "end": v(-15.04, 104.25) * mm});
            skLineSegment(sketch, "E82", {"start": v(-15.04, 104.25) * mm, "end": v(-15.04, 92.25) * mm});
            skLineSegment(sketch, "E83", {"start": v(14.96, 104.25) * mm, "end": v(15, 92.25) * mm});
            skLineSegment(sketch, "E84", {"start": v(-15.04, 92.25) * mm, "end": v(-33.29, 74) * mm});
            skLineSegment(sketch, "E85", {"start": v(15, 92.25) * mm, "end": v(33.07, 74.18) * mm});
            skLineSegment(sketch, "E86", {"start": v(-75.12, 0) * mm, "end": v(74.63, 0) * mm, "construction": true});
            skLineSegment(sketch, "E87.MirrorCS", {"start": v(15, -92.25) * mm, "end": v(33.07, -74.18) * mm});
            skLineSegment(sketch, "E88.MirrorCS", {"start": v(14.96, -104.25) * mm, "end": v(15, -92.25) * mm});
            skLineSegment(sketch, "E89.MirrorCS", {"start": v(0, 0) * mm, "end": v(0, -104.25) * mm, "construction": true});
            skLineSegment(sketch, "E90.MirrorCS", {"start": v(-15.04, -92.25) * mm, "end": v(-33.29, -74) * mm});
            skLineSegment(sketch, "E91.MirrorCS", {"start": v(-15.04, -104.25) * mm, "end": v(-15.04, -92.25) * mm});
            skCircle(sketch, "E92.MirrorC", {"center": v(0, -104.25) * mm, "radius": 6 * mm});
            skArc(sketch, "E93.MirrorCS", {"start": v(14.96, -104.25) * mm, "mid": v(-0.04, -119.2) * mm, "end": v(-15.04, -104.25) * mm});
            skSolve(sketch);
        }
        {
            var Q0;
            Q0=makeQuery(id+"F17.imprint","IMPRINT",FACE,{"disambiguationData":[TD([[makeQuery(id+"F17.imprint","IMPRINT",EDGE,{"derivedFrom":sQuery(id+"F17.wireOp",EDGE,"E80")}),-1.0]])]});
            var Q1;
            {var subQ4=sQuery(id+"F17.wireOp",EDGE,"E88.MirrorCS");Q1=makeQuery(id+"F17.imprint","IMPRINT",FACE,{"disambiguationData":[TD([[makeQuery(id+"F17.imprint","IMPRINT",EDGE,{"derivedFrom":subQ4}),1.0]])]});}
            var Q2;
            Q2=makeQuery(id+"F16.imprint","IMPRINT",FACE,{"disambiguationData":[TD([[makeQuery(id+"F16.imprint","IMPRINT",EDGE,{"derivedFrom":makeQuery(id+"F1.opExtrude","CAP_EDGE",EDGE,{"disambiguationData":[OSD([sQuery(id+"F0.wireOp",EDGE,"E1.bottom")])],"isStart":true})}),1.0]])]});
            extrude(context, id + "F18", {"entities" : qUnion([Q0, Q1, Q2]), "endBound" : BoundingType.SYMMETRIC, "depth" : 6 * mm});
        }
    });
